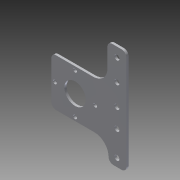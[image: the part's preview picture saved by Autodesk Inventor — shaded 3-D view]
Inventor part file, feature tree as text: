
AUTODESK INVENTOR PART (.ipt)
format: ipt  version: 2013 (Build 170138000, 138)  size: 150,528 bytes
history: native  units: in
note: dims shown in document units (in); Inventor stores cm internally (conversion verified against a paired STEP export)
features: chamfer x2, sketch x2, other x2, sheet_metal_op x1
ambient origin geometry x8: Origin, YZ Plane, XZ Plane, XY Plane, X Axis, Y Axis, Z Axis, Center Point
feature tree (7):
  sheet_metal_op  "Face2"
  chamfer  "Corner Round1"
  chamfer  "Corner Round2"
  sketch  "Sketch1"  dims[d0=2.5in]
  other  "Plate2"
  sketch  "Sketch4"  dims[d1=2.5in d6=0.2in d7=0.2in d8=0.2in d9=0.2in d10=0.12in d11=1.454in d12=1.125in d13=0.5in d15=1.0in d16=0.266in d17=0.266in d18=0.12in d19=0.12in d20=0.0in d23=2.0in d24=1.0in d25=2.25in d26=0.266in d27=0.266in d28=1.325in d29=0.266in d30=0.75in d31=0.25in]
  other  "Cut1"
